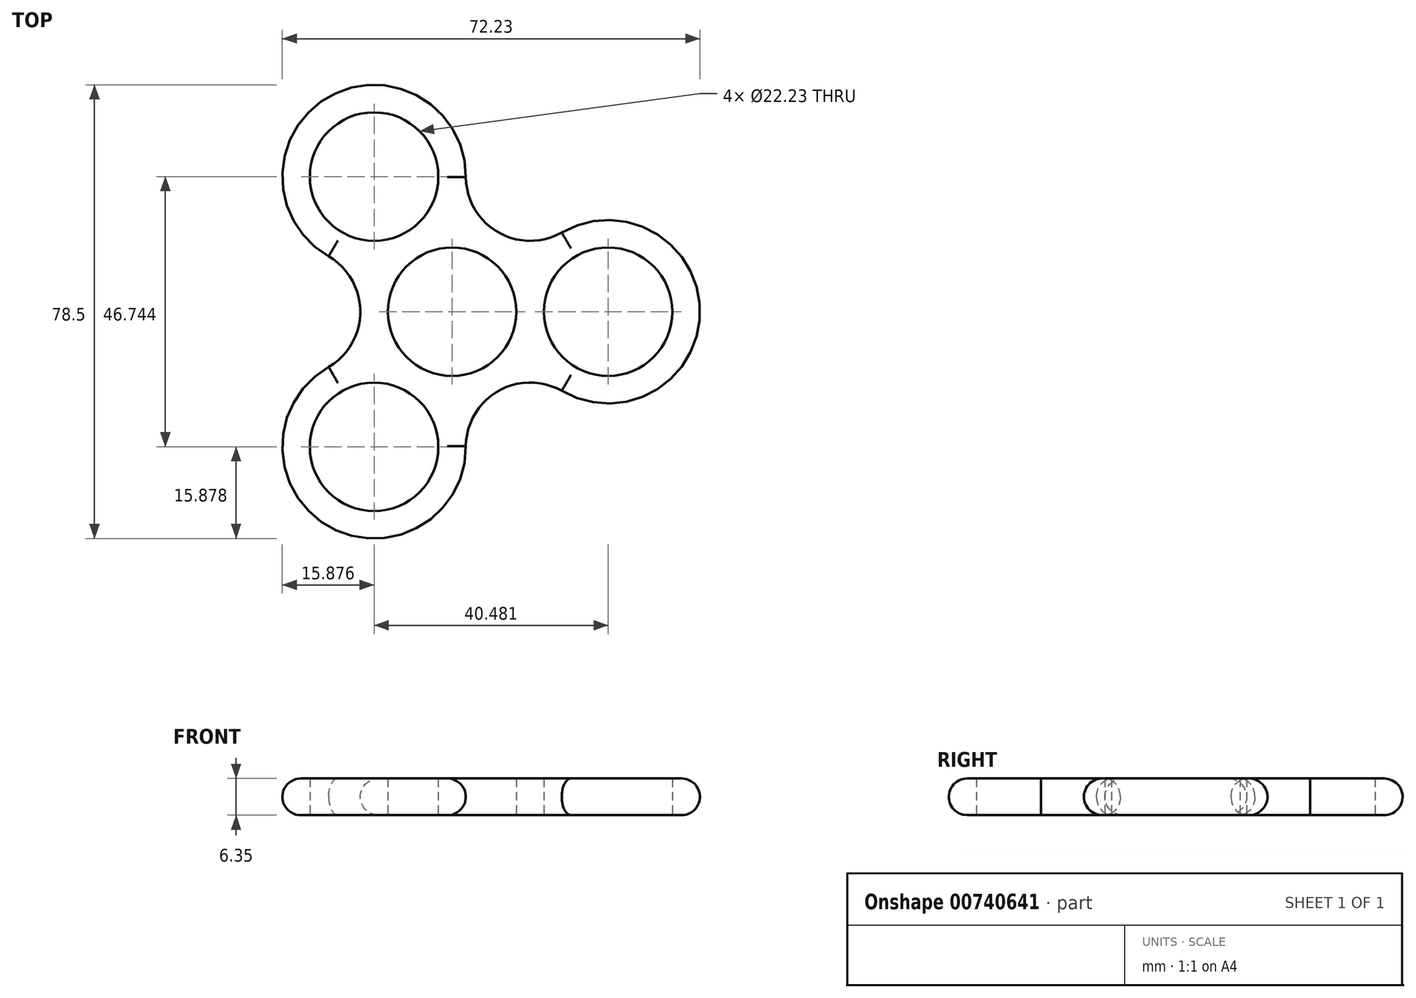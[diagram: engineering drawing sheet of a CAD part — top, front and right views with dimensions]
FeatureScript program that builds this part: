
annotation { "Feature Type Name" : "Feature", "Feature Type Description" : "" }
export const myFeature = defineFeature(function(context is Context, id is Id, definition is map)
    precondition{}
    {
        {
            var Q0;
            Q0=qCreatedBy(makeId("Top.planeOp"),FACE);
            var sketch = newSketch(context, id + "F0", { "sketchPlane" : qUnion([Q0])});
            skPoint(sketch, "E0.center", {"position": v(0, 0) * mm});
            skPoint(sketch, "E1", {"position": v(26.99, 0) * mm});
            skCircle(sketch, "E2", {"center": v(26.99, 0) * mm, "radius": 15.88 * mm});
            skPoint(sketch, "E3.MirrorP", {"position": v(19.14, -13.8) * mm});
            skPoint(sketch, "E4.MirrorP", {"position": v(19.14, 13.8) * mm});
            skPoint(sketch, "E5.1.0", {"position": v(-13.5, 23.37) * mm});
            skCircle(sketch, "E5.1.1", {"center": v(-13.5, 23.37) * mm, "radius": 15.88 * mm});
            skPoint(sketch, "E5.1.2", {"position": v(2.38, 23.47) * mm});
            skPoint(sketch, "E5.1.3", {"position": v(-21.52, 9.67) * mm});
            skPoint(sketch, "E5.2.0", {"position": v(-13.5, -23.37) * mm});
            skCircle(sketch, "E5.2.1", {"center": v(-13.5, -23.37) * mm, "radius": 15.88 * mm});
            skPoint(sketch, "E5.2.2", {"position": v(-21.52, -9.67) * mm});
            skPoint(sketch, "E5.2.3", {"position": v(2.38, -23.47) * mm});
            skPoint(sketch, "E6", {"position": v(15.88, 0) * mm});
            skPoint(sketch, "E7.1.0", {"position": v(7.94, 13.75) * mm});
            skPoint(sketch, "E7.2.0", {"position": v(-7.94, 13.75) * mm});
            skPoint(sketch, "E7.3.0", {"position": v(-15.88, 0) * mm});
            skPoint(sketch, "E7.4.0", {"position": v(-7.94, -13.75) * mm});
            skPoint(sketch, "E7.5.0", {"position": v(7.94, -13.75) * mm});
            skArc(sketch, "E8", {"start": v(19.14, -13.8) * mm, "mid": v(7.94, -13.75) * mm, "end": v(2.38, -23.47) * mm});
            skArc(sketch, "E9", {"start": v(-21.52, -9.67) * mm, "mid": v(-15.88, 0) * mm, "end": v(-21.52, 9.67) * mm});
            skArc(sketch, "E10", {"start": v(2.38, 23.47) * mm, "mid": v(7.94, 13.75) * mm, "end": v(19.14, 13.8) * mm});
            skSolve(sketch);
        }
        {
            var Q0;
            Q0 = qSketchRegion(id + "F0", true);
            extrude(context, id + "F1", {"entities" : qUnion([Q0]), "depth" : 6.35 * mm, "offsetDistance" : 25.4 * mm});
        }
        {
            var Q0;
            Q0=sQuery(id+"F0.wireOp",VERTEX,"E1");
            var Q1;
            Q1=sQuery(id+"F0.wireOp",VERTEX,"E0.center");
            var Q2;
            Q2=sQuery(id+"F0.wireOp",VERTEX,"E5.2.0");
            var Q3;
            Q3=sQuery(id+"F0.wireOp",VERTEX,"E5.1.0");
            var Q4;
            Q4=makeQuery(id+"F1.opExtrude","SWEPT_BODY",BODY,{"disambiguationData":[OSD([sQuery(id+"F0.wireOp",EDGE,"E2"),sQuery(id+"F0.wireOp",EDGE,"E5.1.1"),sQuery(id+"F0.wireOp",EDGE,"E5.2.1"),sQuery(id+"F0.wireOp",EDGE,"E8"),sQuery(id+"F0.wireOp",EDGE,"E9"),sQuery(id+"F0.wireOp",EDGE,"E10")])]});
            hole(context, id + "F2", {"style" : HoleStyle.SIMPLE, "endStyle" : HoleEndStyle.THROUGH, "oppositeDirection" : true, "holeDiameter" : 22.22 * mm, "majorDiameter" : 6.35 * mm, "isTappedThrough" : true, "tappedDepth" : 12.7 * mm, "tapClearance" : 3, "locations" : qUnion([Q0, Q1, Q2, Q3]), "scope" : qUnion([Q4])});
        }
        {
            var Q0;
            Q0=makeQuery(id+"F1.opExtrude","CAP_EDGE",EDGE,{"disambiguationData":[OSD([sQuery(id+"F0.wireOp",EDGE,"E10")])],"isStart":false});
            var Q1;
            Q1=makeQuery(id+"F1.opExtrude","CAP_EDGE",EDGE,{"disambiguationData":[OSD([sQuery(id+"F0.wireOp",EDGE,"E2")])],"isStart":false});
            var Q2;
            Q2=makeQuery(id+"F1.opExtrude","CAP_EDGE",EDGE,{"disambiguationData":[OSD([sQuery(id+"F0.wireOp",EDGE,"E5.2.1")])],"isStart":false});
            var Q3;
            Q3=makeQuery(id+"F1.opExtrude","CAP_EDGE",EDGE,{"disambiguationData":[OSD([sQuery(id+"F0.wireOp",EDGE,"E5.1.1")])],"isStart":false});
            var Q4;
            Q4=makeQuery(id+"F1.opExtrude","CAP_EDGE",EDGE,{"disambiguationData":[OSD([sQuery(id+"F0.wireOp",EDGE,"E5.1.1")])],"isStart":true});
            var Q5;
            Q5=makeQuery(id+"F1.opExtrude","CAP_EDGE",EDGE,{"disambiguationData":[OSD([sQuery(id+"F0.wireOp",EDGE,"E9")])],"isStart":true});
            var Q6;
            Q6=makeQuery(id+"F1.opExtrude","CAP_EDGE",EDGE,{"disambiguationData":[OSD([sQuery(id+"F0.wireOp",EDGE,"E5.2.1")])],"isStart":true});
            var Q7;
            Q7=makeQuery(id+"F1.opExtrude","CAP_EDGE",EDGE,{"disambiguationData":[OSD([sQuery(id+"F0.wireOp",EDGE,"E2")])],"isStart":true});
            fillet(context, id + "F3", {"entities" : qUnion([Q0, Q1, Q2, Q3, Q4, Q5, Q6, Q7]), "radius" : 3.17 * mm, "tangentPropagation" : true, "allowEdgeOverflow" : false});
        }
    });
